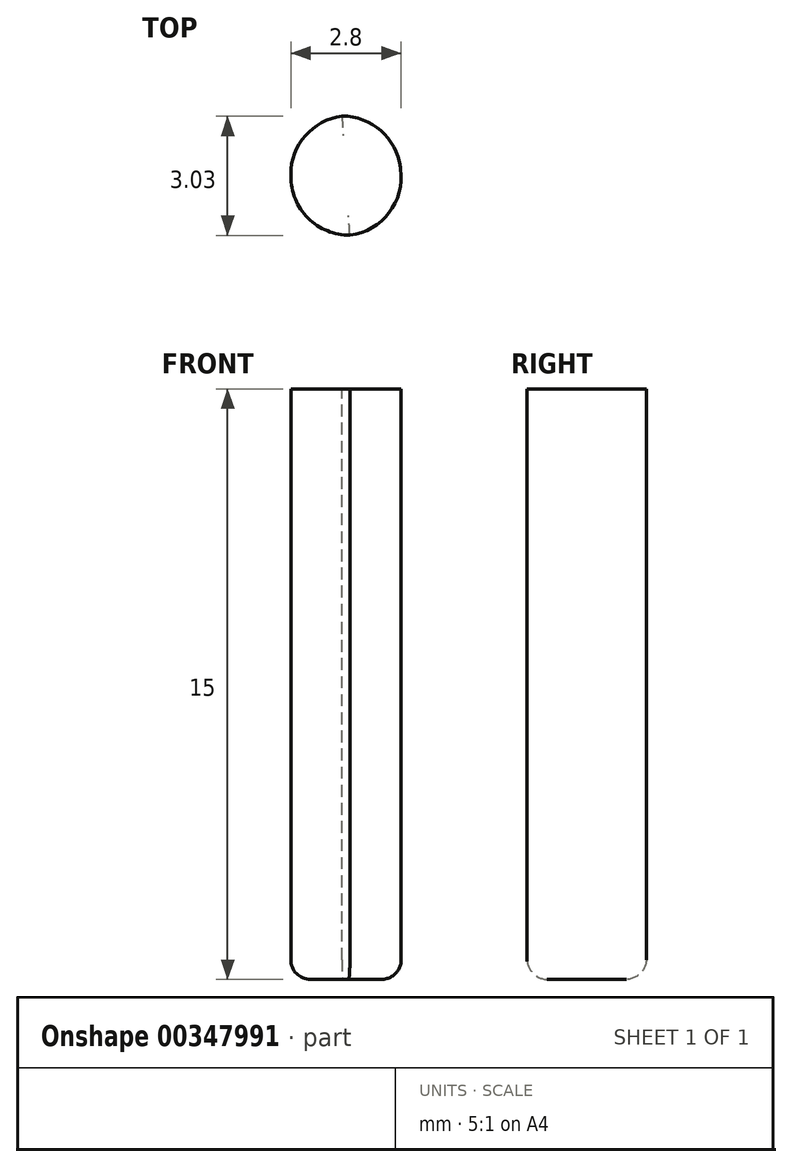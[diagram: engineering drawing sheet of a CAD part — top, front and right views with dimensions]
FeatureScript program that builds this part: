
annotation { "Feature Type Name" : "Feature", "Feature Type Description" : "" }
export const myFeature = defineFeature(function(context is Context, id is Id, definition is map)
    precondition{}
    {
        {
            var Q0;
            Q0=qCreatedBy(makeId("Top.planeOp"),FACE);
            var sketch = newSketch(context, id + "F0", { "sketchPlane" : qUnion([Q0])});
            skArc(sketch, "E0", {"start": v(0, -22.5) * mm, "mid": v(1.5, -22.45) * mm, "end": v(3, -22.3) * mm});
            skLineSegment(sketch, "E1", {"start": v(0, -19.5) * mm, "end": v(0, -22.5) * mm});
            skLineSegment(sketch, "E2", {"start": v(0, -22.5) * mm, "end": v(0, -19.5) * mm});
            skArc(sketch, "E3", {"start": v(3, -22.3) * mm, "mid": v(2.97, -22.11) * mm, "end": v(2.94, -21.92) * mm});
            skLineSegment(sketch, "E4", {"start": v(2.6, -19.33) * mm, "end": v(3, -22.3) * mm});
            skLineSegment(sketch, "E5", {"start": v(3, -22.3) * mm, "end": v(2.6, -19.33) * mm});
            skLineSegment(sketch, "E6", {"start": v(2.6, -19.33) * mm, "end": v(0, -19.5) * mm});
            skPoint(sketch, "E7.orphan", {"position": v(0, 0.56) * mm});
            skSolve(sketch);
        }
        {
            var Q0;
            {var subQ4=sQuery(id+"F0.wireOp",EDGE,"E0");Q0=makeQuery(id+"F0.imprint","IMPRINT",FACE,{"disambiguationData":[TD([[makeQuery(id+"F0.imprint","IMPRINT",EDGE,{"derivedFrom":subQ4}),1.0]])]});}
            extrude(context, id + "F1", {"entities" : qUnion([Q0]), "oppositeDirection" : true, "depth" : 15 * mm});
        }
        {
            var Q0;
            Q0=makeQuery(id+"F1.opExtrude","SWEPT_EDGE",EDGE,{"disambiguationData":[OSD([sQuery(id+"F0.wireOp",EDGE,"E0"),sQuery(id+"F0.wireOp",EDGE,"E3"),sQuery(id+"F0.wireOp",EDGE,"E5")])]});
            var Q1;
            Q1=makeQuery(id+"F1.opExtrude","SWEPT_EDGE",EDGE,{"disambiguationData":[OSD([sQuery(id+"F0.wireOp",EDGE,"E0"),sQuery(id+"F0.wireOp",EDGE,"E2")])]});
            var Q2;
            Q2=makeQuery(id+"F1.opExtrude","SWEPT_EDGE",EDGE,{"disambiguationData":[OSD([sQuery(id+"F0.wireOp",EDGE,"E2"),sQuery(id+"F0.wireOp",EDGE,"E6")])]});
            var Q3;
            Q3=makeQuery(id+"F1.opExtrude","SWEPT_EDGE",EDGE,{"disambiguationData":[OSD([sQuery(id+"F0.wireOp",EDGE,"E5"),sQuery(id+"F0.wireOp",EDGE,"E6")])]});
            fillet(context, id + "F2", {"entities" : qUnion([Q0, Q1, Q2, Q3]), "radius" : 1.5 * mm, "tangentPropagation" : true, "allowEdgeOverflow" : false});
        }
        {
            var Q0;
            Q0=makeQuery(id+"F1.opExtrude","CAP_FACE",FACE,{"disambiguationData":[OSD([sQuery(id+"F0.wireOp",EDGE,"E0"),sQuery(id+"F0.wireOp",EDGE,"E2"),sQuery(id+"F0.wireOp",EDGE,"E5"),sQuery(id+"F0.wireOp",EDGE,"E6")])],"isStart":false});
            fillet(context, id + "F3", {"entities" : qUnion([Q0]), "radius" : 0.5 * mm, "tangentPropagation" : true, "allowEdgeOverflow" : false});
        }
    });
